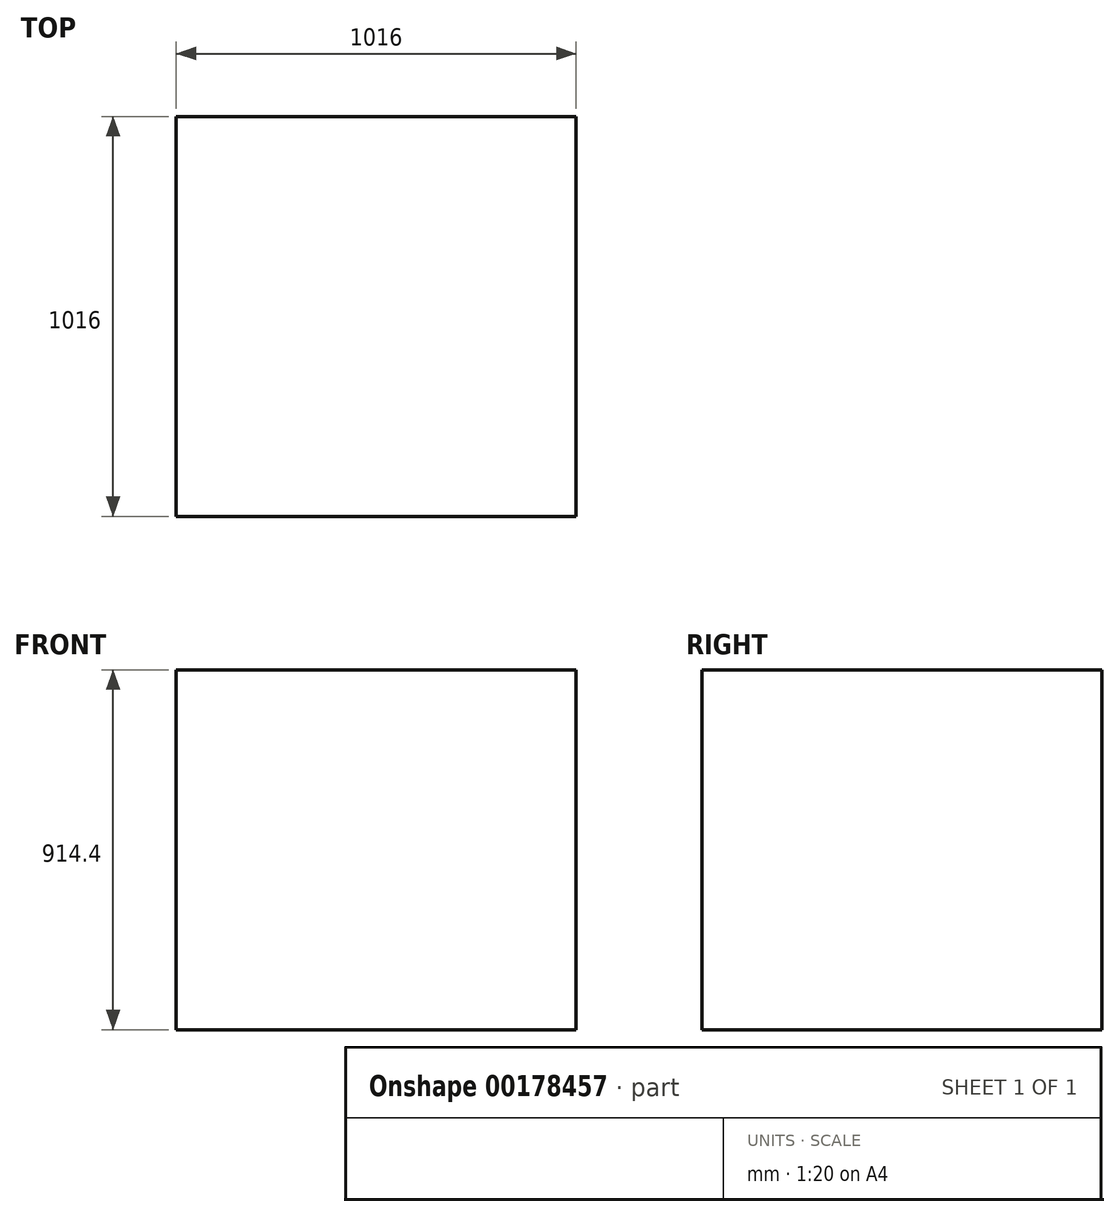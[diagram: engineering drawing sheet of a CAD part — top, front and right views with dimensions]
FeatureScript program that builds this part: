
annotation { "Feature Type Name" : "Feature", "Feature Type Description" : "" }
export const myFeature = defineFeature(function(context is Context, id is Id, definition is map)
    precondition{}
    {
        {
            var Q0;
            Q0=qCreatedBy(makeId("Front.planeOp"),FACE);
            var sketch = newSketch(context, id + "F0", { "sketchPlane" : qUnion([Q0])});
            skLineSegment(sketch, "E0.bottom", {"start": v(508, 457.2) * mm, "end": v(-508, 457.2) * mm});
            skLineSegment(sketch, "E0.top", {"start": v(508, -457.2) * mm, "end": v(-508, -457.2) * mm});
            skLineSegment(sketch, "E0.left", {"start": v(508, 457.2) * mm, "end": v(508, -457.2) * mm});
            skLineSegment(sketch, "E0.right", {"start": v(-508, 457.2) * mm, "end": v(-508, -457.2) * mm});
            skPoint(sketch, "E0.middle", {"position": v(0, 0) * mm});
            skSolve(sketch);
        }
        {
            var Q0;
            Q0=makeQuery(id+"F0.imprint","IMPRINT",FACE,{"disambiguationData":[TD([[makeQuery(id+"F0.imprint","IMPRINT",EDGE,{"derivedFrom":sQuery(id+"F0.wireOp",EDGE,"E0.bottom")}),1.0]])]});
            extrude(context, id + "F1", {"entities" : qUnion([Q0]), "depth" : 508 * mm, "hasSecondDirection" : true, "secondDirectionOppositeDirection" : true, "secondDirectionDepth" : 508 * mm});
        }
    });
